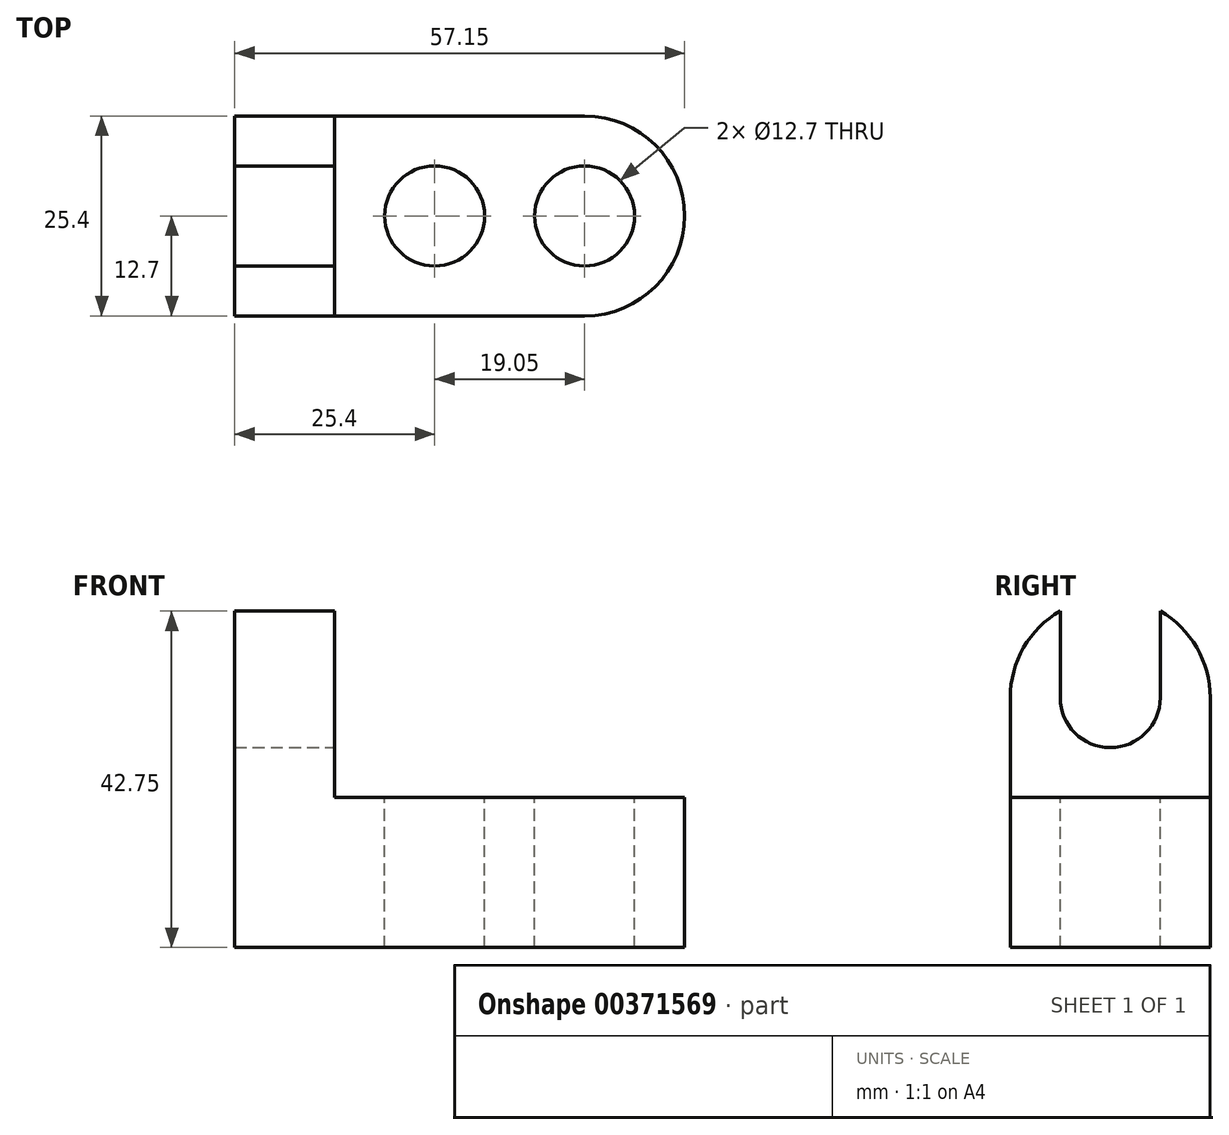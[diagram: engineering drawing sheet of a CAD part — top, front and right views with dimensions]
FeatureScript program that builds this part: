
annotation { "Feature Type Name" : "Feature", "Feature Type Description" : "" }
export const myFeature = defineFeature(function(context is Context, id is Id, definition is map)
    precondition{}
    {
        {
            var Q0;
            Q0=qCreatedBy(makeId("Front.planeOp"),FACE);
            var sketch = newSketch(context, id + "F0", { "sketchPlane" : qUnion([Q0])});
            skLineSegment(sketch, "E0", {"start": v(0, 0) * mm, "end": v(0, 44.45) * mm});
            skLineSegment(sketch, "E1", {"start": v(0, 44.45) * mm, "end": v(12.7, 44.45) * mm});
            skLineSegment(sketch, "E2", {"start": v(12.7, 44.45) * mm, "end": v(12.7, 19.05) * mm});
            skLineSegment(sketch, "E3", {"start": v(12.7, 19.05) * mm, "end": v(57.15, 19.05) * mm});
            skLineSegment(sketch, "E4", {"start": v(57.15, 19.05) * mm, "end": v(57.15, 0) * mm});
            skLineSegment(sketch, "E5", {"start": v(57.15, 0) * mm, "end": v(0, 0) * mm});
            skSolve(sketch);
        }
        {
            var Q0;
            Q0=makeQuery(id+"F0.imprint","IMPRINT",FACE,{"disambiguationData":[TD([[makeQuery(id+"F0.imprint","IMPRINT",EDGE,{"derivedFrom":sQuery(id+"F0.wireOp",EDGE,"E0")}),-1.0]])]});
            extrude(context, id + "F1", {"entities" : qUnion([Q0]), "depth" : 25.4 * mm});
        }
        {
            var Q0;
            Q0=makeQuery(id+"F1.opExtrude","SWEPT_FACE",FACE,{"disambiguationData":[OSD([sQuery(id+"F0.wireOp",EDGE,"E3")])]});
            var sketch = newSketch(context, id + "F2", { "sketchPlane" : qUnion([Q0])});
            skCircle(sketch, "E6", {"center": v(44.45, -12.7) * mm, "radius": 6.35 * mm});
            skCircle(sketch, "E7", {"center": v(25.4, -12.7) * mm, "radius": 6.35 * mm});
            skArc(sketch, "E8", {"start": v(44.45, -25.4) * mm, "mid": v(57.15, -12.7) * mm, "end": v(44.45, 0) * mm});
            skSolve(sketch);
        }
        {
            var Q0;
            Q0=makeQuery(id+"F2.imprint","IMPRINT",FACE,{"disambiguationData":[TD([[makeQuery(id+"F2.imprint","IMPRINT",EDGE,{"derivedFrom":sQuery(id+"F2.wireOp",EDGE,"E7")}),1.0]])]});
            var Q1;
            Q1=makeQuery(id+"F2.imprint","IMPRINT",FACE,{"disambiguationData":[TD([[makeQuery(id+"F2.imprint","IMPRINT",EDGE,{"derivedFrom":sQuery(id+"F2.wireOp",EDGE,"E6")}),1.0]])]});
            var Q2;
            {var subQ0=sQuery(id+"F2.wireOp",EDGE,"E8");var subQ1=sQuery(id+"F0.wireOp",EDGE,"E3");var subQ2=makeQuery(id+"F1.opExtrude","CAP_EDGE",EDGE,{"disambiguationData":[OSD([subQ1])],"isStart":true});var subQ3=makeQuery(id+"F2.imprint","INTERSECT",VERTEX,{"derivedFrom":[subQ2,subQ0]});Q2=makeQuery(id+"F2.imprint","IMPRINT",FACE,{"disambiguationData":[TD([[makeQuery(id+"F2.imprint","IMPRINT",EDGE,{"disambiguationData":[TD([[subQ3,1.0]])],"derivedFrom":subQ0}),-1.0]])]});}
            var Q3;
            {var subQ0=sQuery(id+"F2.wireOp",EDGE,"E8");var subQ1=sQuery(id+"F0.wireOp",EDGE,"E3");var subQ2=makeQuery(id+"F1.opExtrude","CAP_EDGE",EDGE,{"disambiguationData":[OSD([subQ1])],"isStart":false});var subQ3=makeQuery(id+"F2.imprint","INTERSECT",VERTEX,{"derivedFrom":[subQ2,subQ0]});Q3=makeQuery(id+"F2.imprint","IMPRINT",FACE,{"disambiguationData":[TD([[makeQuery(id+"F2.imprint","IMPRINT",EDGE,{"disambiguationData":[TD([[subQ3,-1.0]])],"derivedFrom":subQ0}),-1.0]])]});}
            extrude(context, id + "F3", {"entities" : qUnion([Q0, Q1, Q2, Q3]), "operationType" : NewBodyOperationType.REMOVE, "oppositeDirection" : true, "depth" : 25.4 * mm});
        }
        {
            var Q0;
            Q0=makeQuery(id+"F1.opExtrude","SWEPT_FACE",FACE,{"disambiguationData":[OSD([sQuery(id+"F0.wireOp",EDGE,"E2")])]});
            var sketch = newSketch(context, id + "F4", { "sketchPlane" : qUnion([Q0])});
            skCircle(sketch, "E9", {"center": v(-12.7, 31.75) * mm, "radius": 6.35 * mm});
            skPoint(sketch, "E9.centerSnap0", {"position": v(-12.7, 44.45) * mm});
            skLineSegment(sketch, "E10", {"start": v(-19.05, 31.75) * mm, "end": v(-19.05, 44.45) * mm});
            skLineSegment(sketch, "E11", {"start": v(-6.35, 31.75) * mm, "end": v(-6.35, 44.45) * mm});
            skArc(sketch, "E12", {"start": v(0, 31.75) * mm, "mid": v(-12.7, 44.45) * mm, "end": v(-25.4, 31.75) * mm});
            skSolve(sketch);
        }
        {
            var Q0;
            {var subQ0=sQuery(id+"F4.wireOp",EDGE,"E9");var subQ1=makeQuery(id+"F4.imprint","INTERSECT",VERTEX,{"derivedFrom":[subQ0,sQuery(id+"F4.wireOp",EDGE,"E10")]});Q0=makeQuery(id+"F4.imprint","IMPRINT",FACE,{"disambiguationData":[TD([[makeQuery(id+"F4.imprint","IMPRINT",EDGE,{"disambiguationData":[TD([[subQ1,1.0]])],"derivedFrom":subQ0}),1.0]])]});}
            var Q1;
            {var subQ0=sQuery(id+"F4.wireOp",EDGE,"E10");Q1=makeQuery(id+"F4.imprint","IMPRINT",FACE,{"disambiguationData":[TD([[makeQuery(id+"F4.imprint","IMPRINT",EDGE,{"derivedFrom":subQ0}),-1.0]])]});}
            var Q2;
            {var subQ1=sQuery(id+"F0.wireOp",EDGE,"E2");var subQ4=sQuery(id+"F4.wireOp",EDGE,"E12");var subQ6=makeQuery(id+"F1.opExtrude","CAP_EDGE",EDGE,{"disambiguationData":[OSD([subQ1])],"isStart":false});var subQ7=makeQuery(id+"F4.imprint","INTERSECT",VERTEX,{"derivedFrom":[subQ6,subQ4]});Q2=makeQuery(id+"F4.imprint","IMPRINT",FACE,{"disambiguationData":[TD([[makeQuery(id+"F4.imprint","IMPRINT",EDGE,{"disambiguationData":[TD([[subQ7,1.0]])],"derivedFrom":subQ4}),-1.0]])]});}
            var Q3;
            {var subQ1=sQuery(id+"F0.wireOp",EDGE,"E2");var subQ4=sQuery(id+"F4.wireOp",EDGE,"E12");var subQ6=makeQuery(id+"F1.opExtrude","CAP_EDGE",EDGE,{"disambiguationData":[OSD([subQ1])],"isStart":true});var subQ8=makeQuery(id+"F4.imprint","INTERSECT",VERTEX,{"derivedFrom":[subQ6,subQ4]});Q3=makeQuery(id+"F4.imprint","IMPRINT",FACE,{"disambiguationData":[TD([[makeQuery(id+"F4.imprint","IMPRINT",EDGE,{"disambiguationData":[TD([[subQ8,-1.0]])],"derivedFrom":subQ4}),-1.0]])]});}
            var Q4;
            {var subQ0=sQuery(id+"F4.wireOp",EDGE,"E11");var subQ3=sQuery(id+"F4.wireOp",EDGE,"E12");var subQ4=makeQuery(id+"F4.imprint","INTERSECT",VERTEX,{"derivedFrom":[subQ0,subQ3]});Q4=makeQuery(id+"F4.imprint","IMPRINT",FACE,{"disambiguationData":[TD([[makeQuery(id+"F4.imprint","IMPRINT",EDGE,{"disambiguationData":[TD([[subQ4,-1.0]])],"derivedFrom":subQ0}),1.0]])]});}
            var Q5;
            {var subQ1=sQuery(id+"F4.wireOp",EDGE,"E9");var subQ6=sQuery(id+"F4.wireOp",EDGE,"E10");var subQ7=makeQuery(id+"F4.imprint","INTERSECT",VERTEX,{"derivedFrom":[subQ1,subQ6]});Q5=makeQuery(id+"F4.imprint","IMPRINT",FACE,{"disambiguationData":[TD([[makeQuery(id+"F4.imprint","IMPRINT",EDGE,{"disambiguationData":[TD([[subQ7,1.0]])],"derivedFrom":subQ1}),-1.0]])]});}
            extrude(context, id + "F5", {"entities" : qUnion([Q0, Q1, Q2, Q3, Q4, Q5]), "operationType" : NewBodyOperationType.REMOVE, "oppositeDirection" : true, "depth" : 25.4 * mm});
        }
    });
